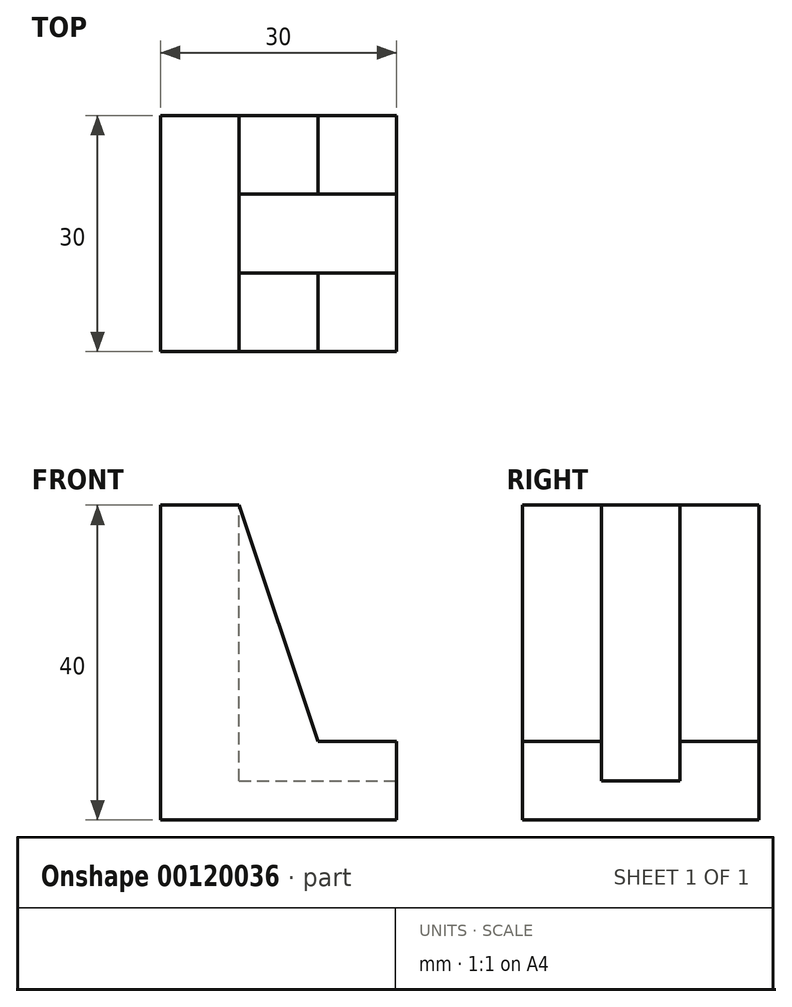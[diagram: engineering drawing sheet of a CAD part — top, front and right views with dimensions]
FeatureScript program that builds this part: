
annotation { "Feature Type Name" : "Feature", "Feature Type Description" : "" }
export const myFeature = defineFeature(function(context is Context, id is Id, definition is map)
    precondition{}
    {
        {
            var Q0;
            Q0=qCreatedBy(makeId("Front.planeOp"),FACE);
            var sketch = newSketch(context, id + "F0", { "sketchPlane" : qUnion([Q0])});
            skLineSegment(sketch, "E0", {"start": v(0, 0) * mm, "end": v(30, 0) * mm});
            skLineSegment(sketch, "E1", {"start": v(30, 0) * mm, "end": v(30, 10) * mm});
            skLineSegment(sketch, "E2", {"start": v(30, 10) * mm, "end": v(20, 10) * mm});
            skLineSegment(sketch, "E3", {"start": v(20, 10) * mm, "end": v(10, 40) * mm});
            skLineSegment(sketch, "E4", {"start": v(10, 40) * mm, "end": v(0, 40) * mm});
            skLineSegment(sketch, "E5", {"start": v(0, 40) * mm, "end": v(0, 0) * mm});
            skSolve(sketch);
        }
        {
            var Q0;
            Q0 = qSketchRegion(id + "F0", true);
            extrude(context, id + "F1", {"entities" : qUnion([Q0]), "depth" : 30 * mm});
        }
        {
            var Q0;
            Q0=makeQuery(id+"F1.opExtrude","SWEPT_FACE",FACE,{"disambiguationData":[OSD([sQuery(id+"F0.wireOp",EDGE,"E4")])]});
            var sketch = newSketch(context, id + "F2", { "sketchPlane" : qUnion([Q0])});
            skLineSegment(sketch, "E6.bottom", {"start": v(10, -10) * mm, "end": v(39.71, -10) * mm});
            skLineSegment(sketch, "E6.top", {"start": v(10, -20) * mm, "end": v(39.71, -20) * mm});
            skLineSegment(sketch, "E6.left", {"start": v(10, -10) * mm, "end": v(10, -20) * mm});
            skLineSegment(sketch, "E6.right", {"start": v(39.71, -10) * mm, "end": v(39.71, -20) * mm});
            skSolve(sketch);
        }
        {
            var Q0;
            Q0 = qSketchRegion(id + "F2", true);
            extrude(context, id + "F3", {"entities" : qUnion([Q0]), "operationType" : NewBodyOperationType.REMOVE, "oppositeDirection" : true, "depth" : 35 * mm});
        }
    });
